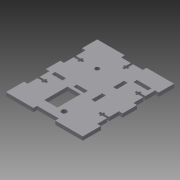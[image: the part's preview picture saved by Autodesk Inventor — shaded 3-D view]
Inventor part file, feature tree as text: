
AUTODESK INVENTOR PART (.ipt)
format: ipt  version: 2014 (Build 180170000, 170)  size: 311,296 bytes
history: native  units: mm
features: reference x11, extrude x8, sketch x8, other x6, plane x4
ambient origin geometry x8: Origin, YZ Plane, XZ Plane, XY Plane, X Axis, Y Axis, Z Axis, Center Point
bodies: 实体1 (feature_tree)
feature tree (37):
  extrude  "拉伸1"  Depth=50.0mm
  sketch  "草图3"  dims[d4=30.0mm d5=33.0mm]
  plane  "工作平面1"
  extrude  "拉伸2"  Depth=33.0mm
  sketch  "草图4"  dims[d6=30.0mm d7=33.0mm]
  plane  "工作平面2"
  extrude  "拉伸3"  Depth=33.0mm
  sketch  "草图5"  dims[d8=53.0mm d9=15.0mm]
  plane  "工作平面3"
  extrude  "拉伸4"  Depth=15.0mm
  sketch  "草图6"  dims[d10=5.0mm d11=15.0mm]
  plane  "工作平面4"
  extrude  "拉伸5"  Depth=15.0mm
  extrude  "拉伸6"  Depth=5.0mm
  extrude  "拉伸7"  Depth=54.0mm
  extrude  "拉伸8"  Depth=15.0mm
  sketch  "草图1"  dims[d0=16.0mm d3=50.0mm]
  reference  "参考1"
  reference  "参考2"
  reference  "参考3"
  reference  "参考5"
  reference  "参考6"
  sketch  "草图7"  dims[d12=5.0mm d13=5.0mm]
  reference  "参考7"
  reference  "参考8"
  reference  "参考9"
  reference  "参考10"
  reference  "参考11"
  other  "slot"
  sketch  "草图8"  dims[d14=15.0mm d15=54.0mm]
  reference  "参考12"
  sketch  "草图9"  dims[d16=5.0mm d17=15.0mm d18=5.0mm d19=15.0mm d20=5.0mm d21=15.0mm d22=6.0mm d23=5.0mm d24=0.0mm d25=5.0mm d26=0.0mm d27=5.0mm d28=0.0mm d29=5.0mm d30=0.0mm d31=5.0mm d32=0.0mm d33=3.0mm d34=12.0mm d35=6.5mm d36=2.4mm d37=8.0mm d38=5.0mm d39=0.0mm d40=18.0mm d41=32.0mm d42=28.0mm d43=4.0mm d44=5.0mm d45=0.0mm d46=7.2mm d47=10.0mm d48=0.0mm]
  other  "slot:1"
  other  "slot:2"
  other  "slot:3"
  other  "slot:4"
  other  "slot:5"
